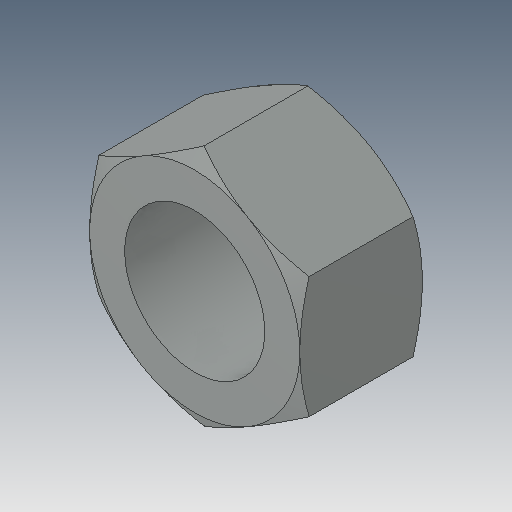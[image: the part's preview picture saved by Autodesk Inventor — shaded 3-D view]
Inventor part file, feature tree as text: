
AUTODESK INVENTOR PART (.ipt)
format: ipt  version: 2023.5 (Build 275446000, 446)  size: 119,808 bytes
history: native  units: in
note: dims shown in document units (in); Inventor stores cm internally (conversion verified against a paired STEP export)
features: mirror x1
ambient origin geometry x8: Origin, YZ Plane, XZ Plane, XY Plane, X Axis, Y Axis, Z Axis, Center Point
bodies: Solid1 (feature_tree)
feature tree (1):
  mirror  "Mirror1"
